# Revit family: RSH_10_11_12_14_16_18_s200
name_source: partatom
category: Generic Models
units: mm (PartAtom-declared; Revit-internal decimal feet)

## family parameters
Always vertical = No
Can host rebar = Yes
Cut with Voids When Loaded = No
Part Type = Normal
Room Calculation Point = No
Round Connector Dimension = Use Diameter
Shared = No
Work Plane-Based = Yes

## types (8) — shared parameters
CenterToCenter_2 = 210 mm  [stored 0.688976 ft]
Default Elevation = 1219 mm
Manufacturer = Recostal

## per-type parameters (varying)
| type | Diameter Rebar | Length rebar | Model | Width Box | Width rebar |
| RSH 12 - 10 - 200mm | 10 mm  [stored 0.0328084 ft] | 540 mm  [stored 1.77165 ft] | RSH 12_10_200 | 79 mm | 65 mm  [stored 0.213255 ft] |
| RSH 10 - 10 - 200mm | 10 mm  [stored 0.0328084 ft] | 540 mm  [stored 1.77165 ft] | RSH 10_10_200 | 59 mm | 45 mm  [stored 0.147638 ft] |
| RSH 10 - 12 - 200mm | 12 mm  [stored 0.0393701 ft] | 610 mm  [stored 2.00131 ft] | RSH 10_12_200 | 59 mm | 45 mm  [stored 0.147638 ft] |
| RSH 12 - 12 - 200mm | 12 mm  [stored 0.0393701 ft] | 610 mm  [stored 2.00131 ft] | RSH 12_12_200 | 79 mm | 65 mm  [stored 0.213255 ft] |
| RSH 11 - 10 - 200mm | 10 mm  [stored 0.0328084 ft] | 540 mm  [stored 1.77165 ft] | RSH 11_10_200 | 69 mm | 55 mm  [stored 0.180446 ft] |
| RSH 11 - 12 - 200mm | 12 mm  [stored 0.0393701 ft] | 610 mm  [stored 2.00131 ft] | RSH 11_10_200 | 69 mm | 55 mm  [stored 0.180446 ft] |
| RSH 14 - 10 - 200mm | 10 mm  [stored 0.0328084 ft] | 540 mm  [stored 1.77165 ft] | RSH 14_10_200 | 99 mm | 85 mm  [stored 0.278871 ft] |
| RSH 14 - 12 - 200mm | 12 mm  [stored 0.0393701 ft] | 610 mm  [stored 2.00131 ft] | RSH 14_10_200 | 99 mm | 85 mm  [stored 0.278871 ft] |

note: [stored X ft] marks values corroborated as IEEE doubles in the binary element streams (Revit-internal decimal feet)

## geometry (parser evidence)
native form markers: Sweep x17
no freeform markers — native parametric forms only
